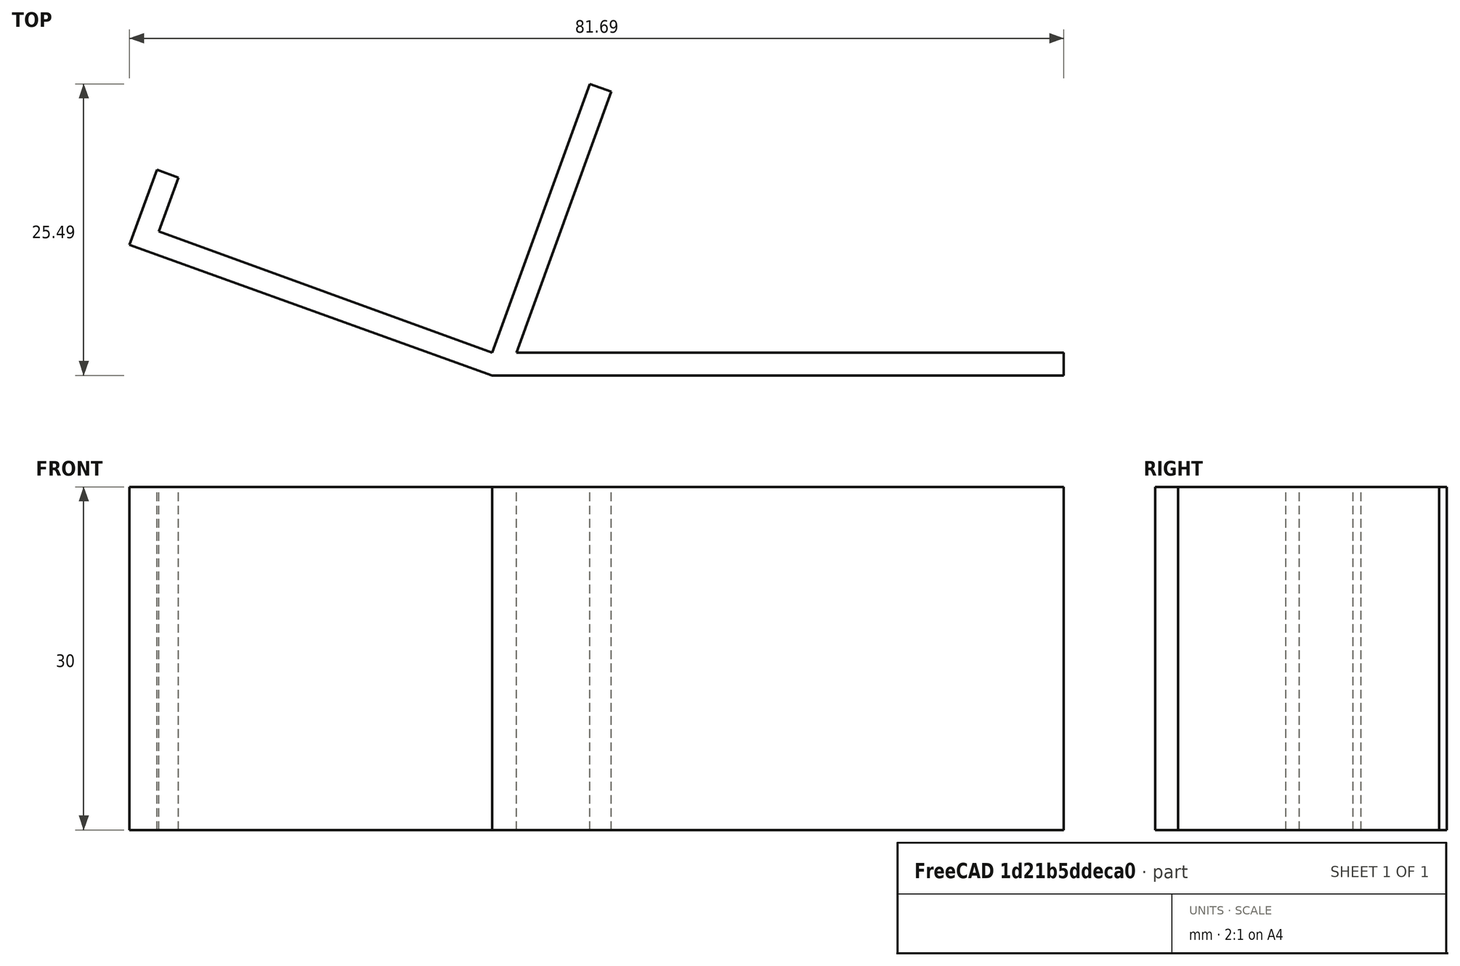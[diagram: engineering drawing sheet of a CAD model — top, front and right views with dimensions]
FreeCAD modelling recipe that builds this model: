
FCSTD DOCUMENT  (FreeCAD 1.0R38806 (Git))
Label: Frame75Stand
License: All rights reserved
LicenseURL: https://en.wikipedia.org/wiki/All_rights_reserved
objects: Sketcher::SketchObject×1, PartDesign::Pad×1, PartDesign::Body×1
note: 6 computed .brp shape members not serialized (recipe doc carries the construction recipe); baked Part::Feature solids carry a one-line shape summary decoded from their .brp

FEATURE [Sketcher::SketchObject] Sketch  label="StandS"
  ArcFitTolerance = 0
  AttachmentSupport = -> [XY_Plane]
  FullyConstrained = true
  MakeInternals = false
  MapMode = 5
  sketch-geometry (11):
    g0: LineSegment StartX=0 StartY=0 StartZ=0 EndX=50 EndY=0 EndZ=0
    g1: LineSegment StartX=50 StartY=0 StartZ=0 EndX=50 EndY=2 EndZ=0
    g2: LineSegment StartX=50 StartY=2 StartZ=0 EndX=2.12837 EndY=2 EndZ=0
    g3: LineSegment StartX=2.12837 StartY=2 StartZ=0 EndX=10.4299 EndY=24.8083 EndZ=0
    g4: LineSegment StartX=10.4299 StartY=24.8083 StartZ=0 EndX=8.55052 EndY=25.4923 EndZ=0
    g5: LineSegment StartX=8.55052 StartY=25.4923 StartZ=0 EndX=1.40767e-05 EndY=2 EndZ=0
    g6: LineSegment StartX=1.40767e-05 StartY=2 StartZ=0 EndX=-29.1305 EndY=12.6026 EndZ=0
    g7: LineSegment StartX=-31.6939 StartY=11.4073 StartZ=0 EndX=0 EndY=0 EndZ=0
    g8: LineSegment StartX=-31.6939 StartY=11.4073 StartZ=0 EndX=-29.2997 EndY=17.9851 EndZ=0
    g9: LineSegment StartX=-29.2997 StartY=17.9851 StartZ=0 EndX=-27.4204 EndY=17.3011 EndZ=0
    g10: LineSegment StartX=-27.4204 StartY=17.3011 StartZ=0 EndX=-29.1305 EndY=12.6026 EndZ=0
  constraints (32):
    c: Horizontal(g0)
    c: Coincident(g0,g1)
    c: Vertical(g1)
    c: Coincident(g1,g2)
    c: Horizontal(g2)
    c: Coincident(g2,g3)
    c: Coincident(g3,g4)
    c: Coincident(g4,g5)
    c: Coincident(g5,g6)
    c: Coincident(g0,g7)
    c: Coincident(g0,g-1)
    c: Distance(g4) = 2
    c: Distance(g1) = 2
    c: Distance(g0) = 50
    c: Coincident(g8,g9)
    c: Coincident(g9,g10)
    c: Coincident(g6,g10)
    c: Coincident(g7,g8)
    c: Distance(g9) = 2
    c: Distance(g10) = 5
    c: Distance(g5) = 25
    c: Angle(g5,g6) = 1.5708
    c: DistanceY(g2,g5) = 0
    c: Angle(g6,g10) = 1.5708
    c: Distance(g8) = 7
    c: Angle(g9,g10) = 1.5708
    c: Angle(g8,g9) = 1.5708
    c: Angle(g5,g4) = 1.5708
    c: Angle(g4,g3) = 1.5708
    c: Distance(g6) = 31
    c: Distance(g0,g5) = 2
    c: Angle(g2,g3) = 1.22173
FEATURE [PartDesign::Pad] Pad  label="Stand"
  Direction = (0,0,1)
  Length = 30
  Length2 = 10
  Profile = -> Sketch
  ReferenceAxis = -> Sketch [N_Axis]
  Suppressed = false
  Type = 0
FEATURE [PartDesign::Body] Body
  AllowCompound = false
  Group = -> [Sketch,Pad]
  Origin = -> Origin
  Tip = -> Pad
